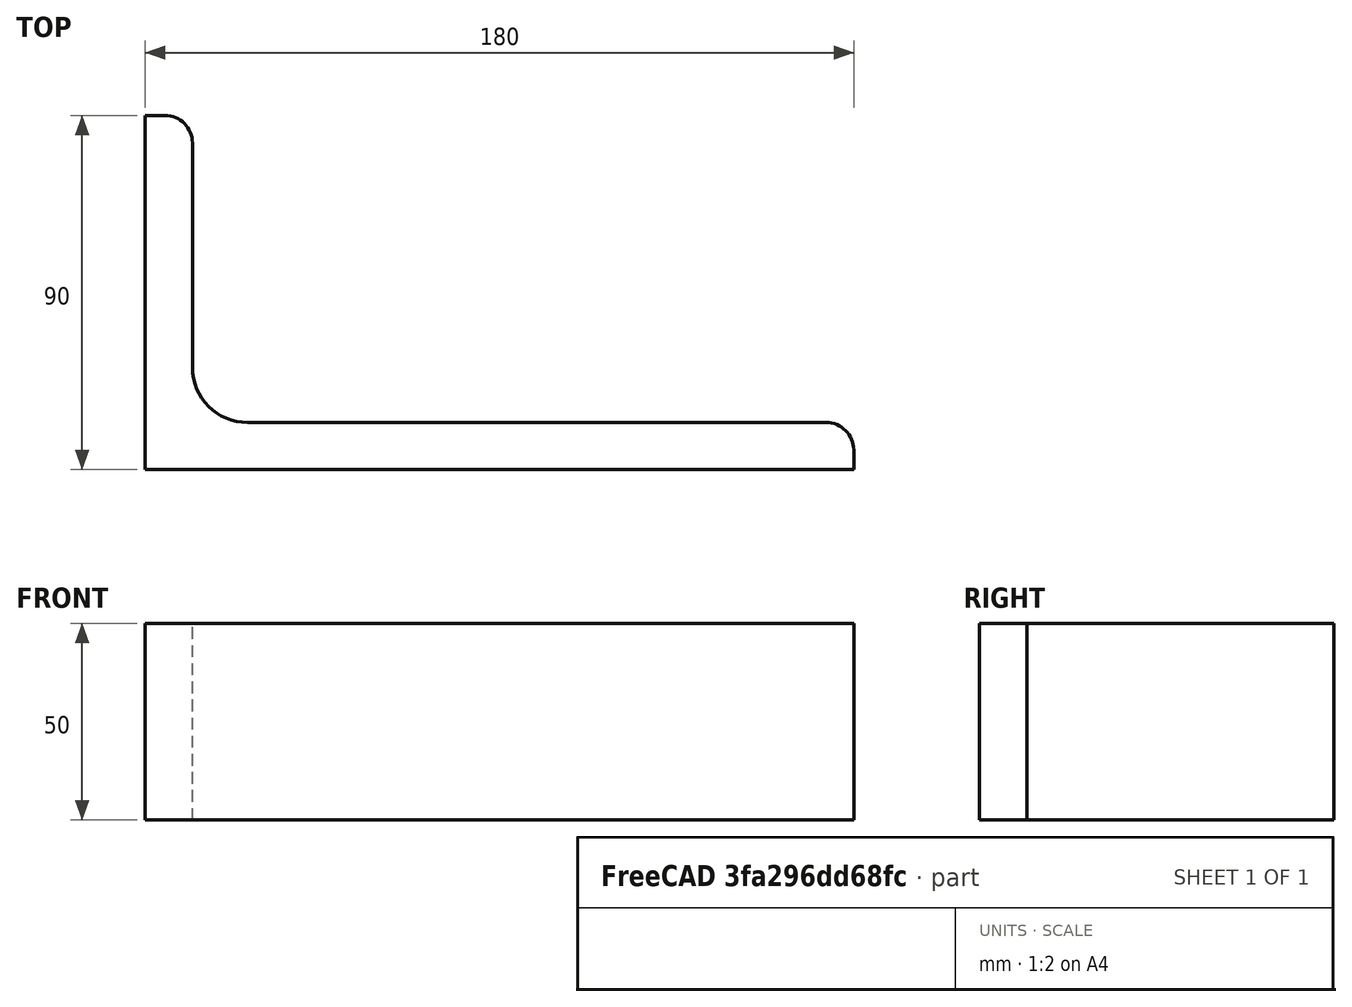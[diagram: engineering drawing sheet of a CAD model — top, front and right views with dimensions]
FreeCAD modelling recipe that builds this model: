
FCSTD DOCUMENT  (FreeCAD 0.15R4671 (Git))
Label: Angle Bar 180x90x12 EN10056 S235JR
License: All rights reserved
LicenseURL: http://en.wikipedia.org/wiki/All_rights_reserved
objects: Sketcher::SketchObject×1, Part::Extrusion×1
note: 2 computed .brp shape members not serialized (recipe doc carries the construction recipe); baked Part::Feature solids carry a one-line shape summary decoded from their .brp

FEATURE [Sketcher::SketchObject] Sketch
  sketch-geometry (9):
    g0: LineSegment StartX=0 StartY=0 StartZ=0 EndX=180 EndY=0 EndZ=0
    g1: LineSegment StartX=180 StartY=0 StartZ=0 EndX=180 EndY=5 EndZ=0
    g2: LineSegment StartX=173 StartY=12 StartZ=0 EndX=26 EndY=12 EndZ=0
    g3: LineSegment StartX=0 StartY=0 StartZ=0 EndX=0 EndY=90 EndZ=0
    g4: LineSegment StartX=0 StartY=90 StartZ=0 EndX=5 EndY=90 EndZ=0
    g5: LineSegment StartX=12 StartY=83 StartZ=0 EndX=12 EndY=26 EndZ=0
    g6: ArcOfCircle CenterX=26 CenterY=26 CenterZ=0 NormalX=0 NormalY=0 NormalZ=1 Radius=14 StartAngle=3.14159 EndAngle=4.71239
    g7: ArcOfCircle CenterX=5 CenterY=83 CenterZ=0 NormalX=0 NormalY=0 NormalZ=1 Radius=7 StartAngle=0 EndAngle=1.5708
    g8: ArcOfCircle CenterX=173 CenterY=5 CenterZ=0 NormalX=0 NormalY=0 NormalZ=1 Radius=7 StartAngle=0 EndAngle=1.5708
  constraints (23):
    c: Coincident(g0,g-1)
    c: Horizontal(g0)
    c: Coincident(g1,g0)
    c: Vertical(g1)
    c: Horizontal(g2)
    c: Coincident(g3,g-1)
    c: Vertical(g3)
    c: Coincident(g4,g3)
    c: Horizontal(g4)
    c: Vertical(g5)
    c: Tangent(g5,g6) = -1.5708
    c: Tangent(g2,g6) = 1.5708
    c: Tangent(g4,g7) = 1.5708
    c: Tangent(g5,g7) = 1.5708
    c: Tangent(g2,g8) = -1.5708
    c: Tangent(g1,g8) = -1.5708
    c: DistanceX(g0) = 180
    c: DistanceY(g3) = 90
    c: DistanceY(g0,g2) = 12
    c: DistanceX(g3,g5) = 12
    c: Radius(g6) = 14
    c: Radius(g8) = 7
    c: Radius(g7) = 7
FEATURE [Part::Extrusion] Extrude  label="Angle Bar 180x90x12 EN10056 S235JR"
  Base = -> Sketch
  Dir = (0,0,50)
  Solid = true
